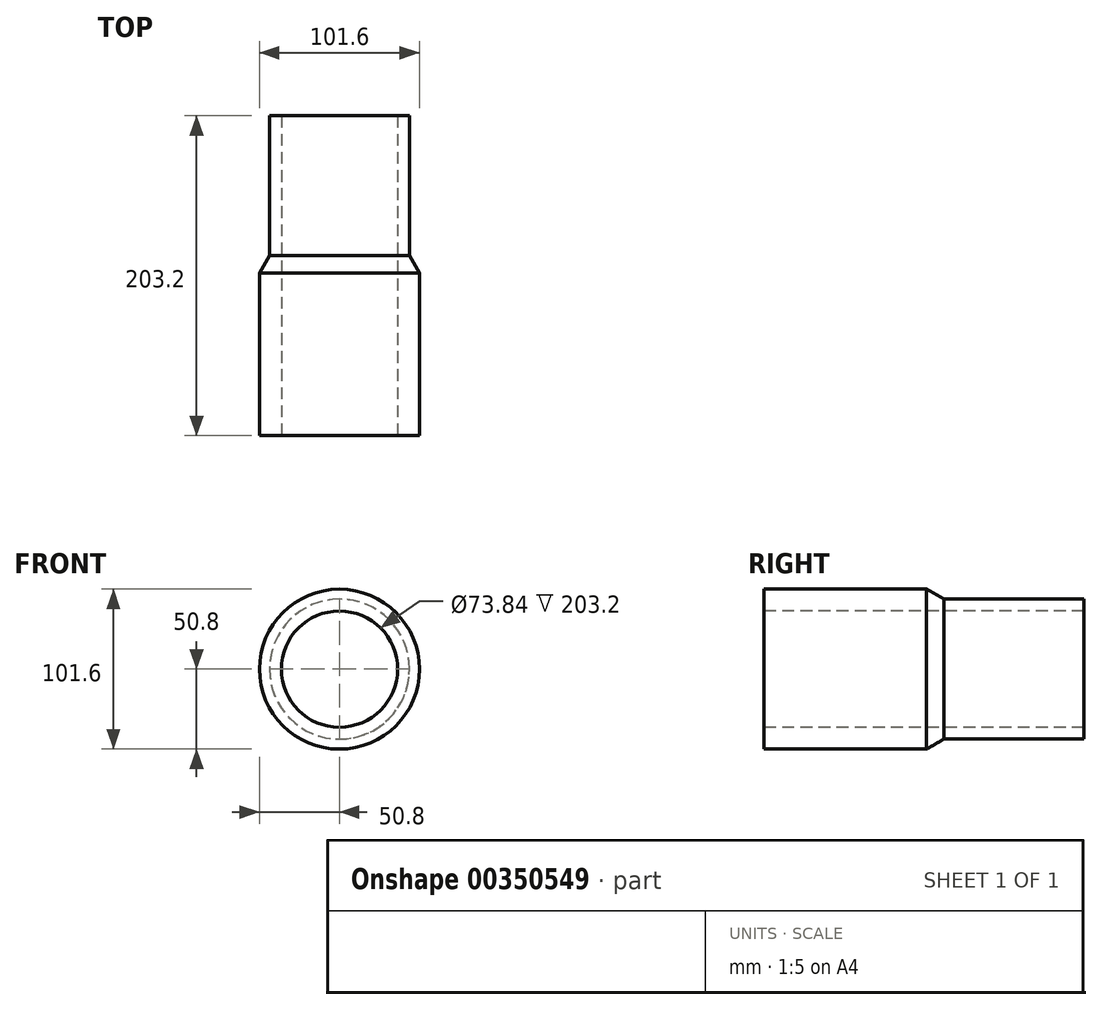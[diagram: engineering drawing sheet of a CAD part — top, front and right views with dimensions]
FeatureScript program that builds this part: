
annotation { "Feature Type Name" : "Feature", "Feature Type Description" : "" }
export const myFeature = defineFeature(function(context is Context, id is Id, definition is map)
    precondition{}
    {
        {
            var Q0;
            Q0=qCreatedBy(makeId("Front.planeOp"),FACE);
            var sketch = newSketch(context, id + "F0", { "sketchPlane" : qUnion([Q0])});
            skCircle(sketch, "E0", {"center": v(0, 0) * mm, "radius": 50.8 * mm});
            skSolve(sketch);
        }
        {
            var Q0;
            Q0 = qSketchRegion(id + "F0", true);
            extrude(context, id + "F1", {"entities" : qUnion([Q0]), "depth" : 203.2 * mm});
        }
        {
            var Q0;
            Q0=qCreatedBy(makeId("Top.planeOp"),FACE);
            var sketch = newSketch(context, id + "F2", { "sketchPlane" : qUnion([Q0])});
            skLineSegment(sketch, "E1", {"start": v(44.45, 0) * mm, "end": v(44.45, -88.9) * mm});
            skLineSegment(sketch, "E2", {"start": v(44.45, -88.9) * mm, "end": v(89.64, -167.16) * mm});
            skLineSegment(sketch, "E3", {"start": v(89.64, -167.16) * mm, "end": v(89.64, 0) * mm});
            skLineSegment(sketch, "E4", {"start": v(89.64, 0) * mm, "end": v(44.45, 0) * mm});
            skSolve(sketch);
        }
        {
            var Q0;
            Q0 = qSketchRegion(id + "F2", true);
            var Q1;
            Q1=makeQuery(id+"F1.opExtrude","SWEPT_FACE",FACE,{"disambiguationData":[OSD([sQuery(id+"F0.wireOp",EDGE,"E0")])]});
            revolve(context, id + "F3", {"operationType" : NewBodyOperationType.REMOVE, "entities" : qUnion([Q0]), "axis" : qUnion([Q1]), "revolveType" : RevolveType.FULL, "oppositeDirection" : true});
        }
        {
            var Q0;
            Q0=makeQuery(id+"F1.opExtrude","CAP_FACE",FACE,{"disambiguationData":[OSD([sQuery(id+"F0.wireOp",EDGE,"E0")])],"isStart":false});
            var sketch = newSketch(context, id + "F4", { "sketchPlane" : qUnion([Q0])});
            skCircle(sketch, "E5", {"center": v(0, 0) * mm, "radius": 36.92 * mm});
            skSolve(sketch);
        }
        {
            var Q0;
            Q0 = qSketchRegion(id + "F4", true);
            extrude(context, id + "F5", {"entities" : qUnion([Q0]), "operationType" : NewBodyOperationType.REMOVE, "oppositeDirection" : true, "depth" : 203.2 * mm});
        }
    });
